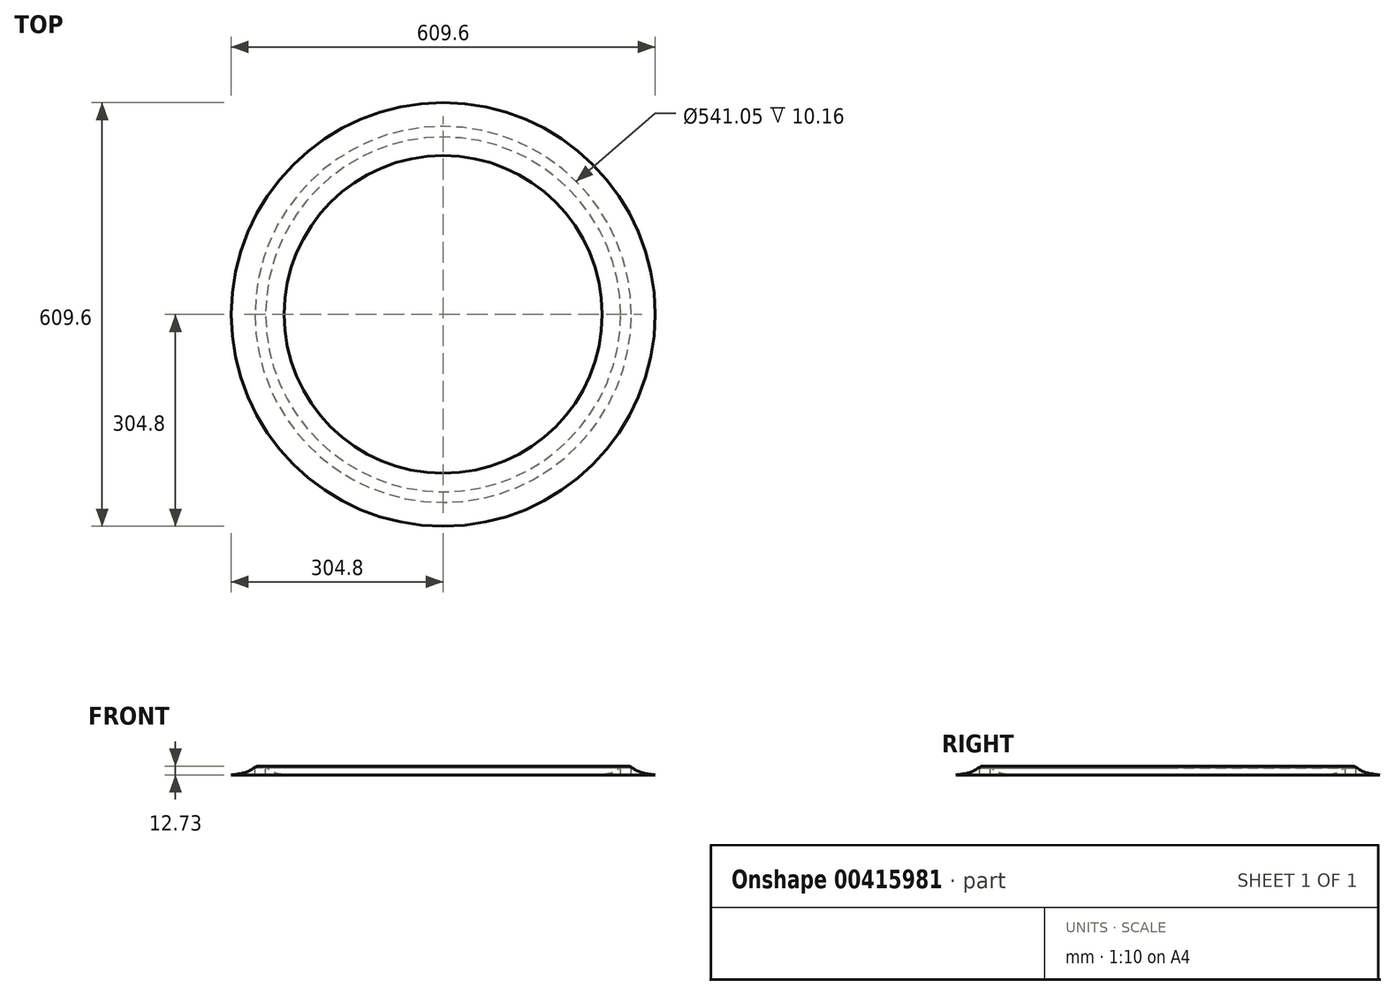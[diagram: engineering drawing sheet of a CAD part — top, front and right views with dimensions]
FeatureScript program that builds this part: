
annotation { "Feature Type Name" : "Feature", "Feature Type Description" : "" }
export const myFeature = defineFeature(function(context is Context, id is Id, definition is map)
    precondition{}
    {
        {
            var Q0;
            Q0=qCreatedBy(makeId("Front.planeOp"),FACE);
            var sketch = newSketch(context, id + "F0", { "sketchPlane" : qUnion([Q0])});
            skLineSegment(sketch, "E0", {"start": v(228.6, 0) * mm, "end": v(304.8, 0) * mm});
            skFitSpline(sketch, "E1", {"points": [v(304.8, 0) * mm, v(288.34, 2.53) * mm, v(276.3, 7.33) * mm, v(268.14, 12.12) * mm, v(262.2, 12.7) * mm, v(255.61, 11.47) * mm, v(247.76, 5.17) * mm, v(240.95, 2.53) * mm, v(228.6, 0) * mm], "startDerivative": vector(-103.23, 12.9) * mm, "endDerivative": vector(-95.01, -15.62) * mm});
            skLineSegment(sketch, "E2", {"start": v(270.53, 0) * mm, "end": v(270.53, 10.16) * mm});
            skLineSegment(sketch, "E3", {"start": v(270.53, 10.16) * mm, "end": v(255.29, 10.16) * mm});
            skLineSegment(sketch, "E4", {"start": v(255.29, 10.16) * mm, "end": v(255.29, 0) * mm});
            skLineSegment(sketch, "E5", {"start": v(255.29, 0) * mm, "end": v(270.53, 0) * mm});
            skLineSegment(sketch, "E6", {"start": v(0, 48.03) * mm, "end": v(0, -38.43) * mm});
            skSolve(sketch);
        }
        {
            var Q0;
            {var subQ1=sQuery(id+"F0.wireOp",EDGE,"E1");Q0=makeQuery(id+"F0.imprint","IMPRINT",FACE,{"disambiguationData":[TD([[makeQuery(id+"F0.imprint","IMPRINT",EDGE,{"derivedFrom":subQ1}),1.0]])]});}
            var Q1;
            Q1=sQuery(id+"F0.wireOp",EDGE,"E6");
            revolve(context, id + "F1", {"entities" : qUnion([Q0]), "axis" : qUnion([Q1]), "revolveType" : RevolveType.FULL});
        }
    });
